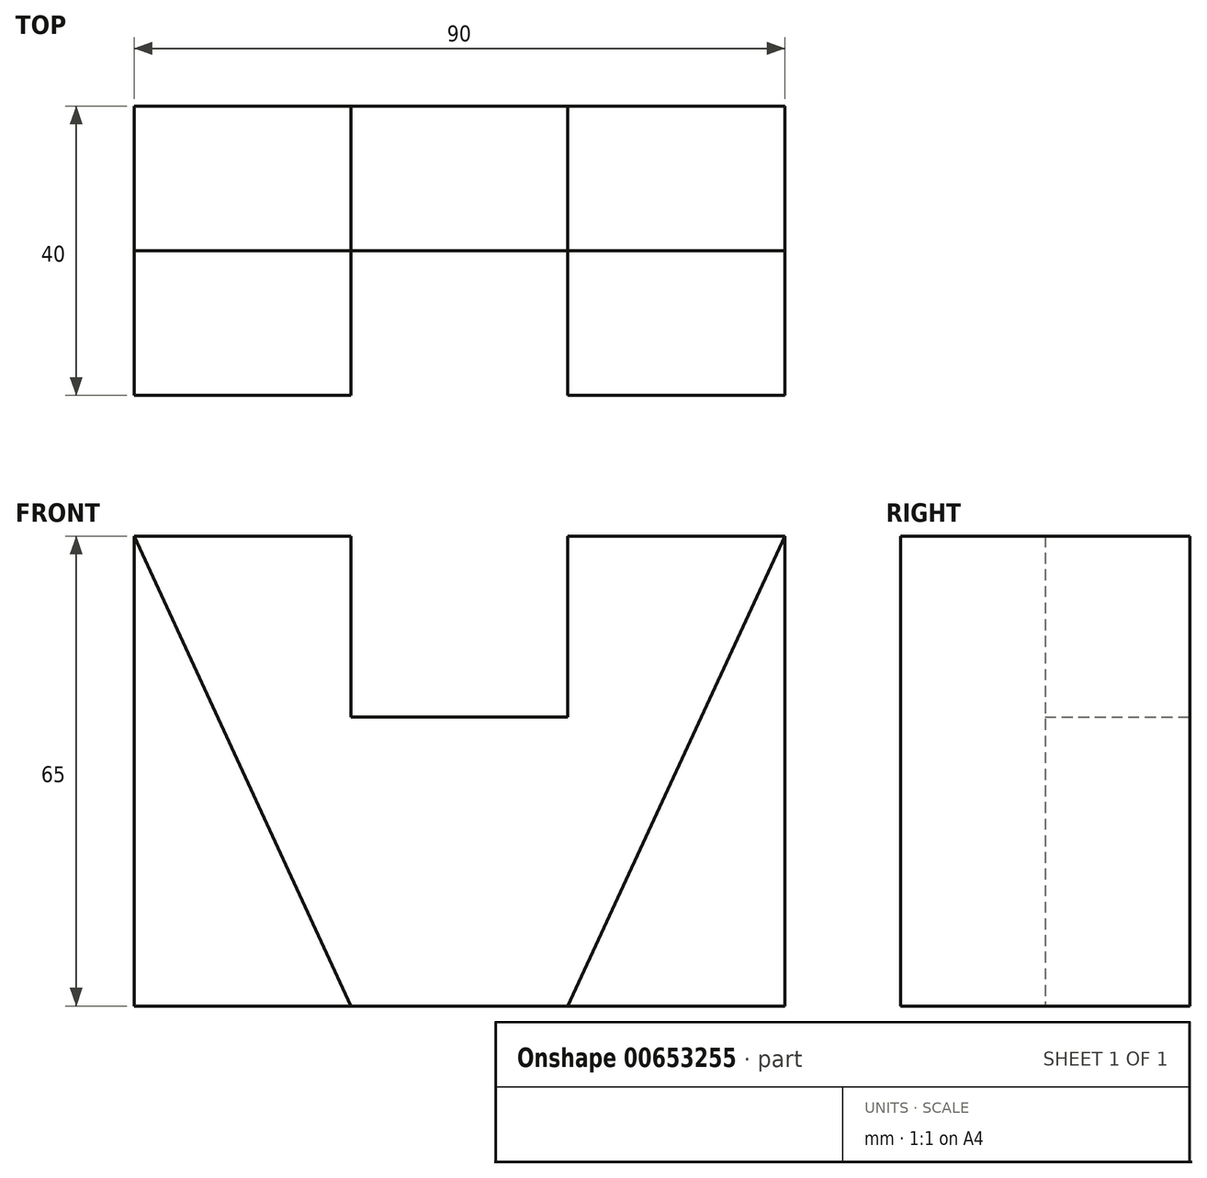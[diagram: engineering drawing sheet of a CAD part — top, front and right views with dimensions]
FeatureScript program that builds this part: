
annotation { "Feature Type Name" : "Feature", "Feature Type Description" : "" }
export const myFeature = defineFeature(function(context is Context, id is Id, definition is map)
    precondition{}
    {
        {
            var Q0;
            Q0=qCreatedBy(makeId("Front.planeOp"),FACE);
            var sketch = newSketch(context, id + "F0", { "sketchPlane" : qUnion([Q0])});
            skLineSegment(sketch, "E0.bottom", {"start": v(-45, 32.5) * mm, "end": v(-15, 32.5) * mm});
            skLineSegment(sketch, "E0.top", {"start": v(-45, -32.5) * mm, "end": v(45, -32.5) * mm});
            skLineSegment(sketch, "E0.left", {"start": v(-45, 32.5) * mm, "end": v(-45, -32.5) * mm});
            skLineSegment(sketch, "E0.right", {"start": v(45, 32.5) * mm, "end": v(45, -32.5) * mm});
            skPoint(sketch, "E0.middle", {"position": v(0, 0) * mm});
            skLineSegment(sketch, "E1.top", {"start": v(-15, 7.5) * mm, "end": v(15, 7.5) * mm});
            skLineSegment(sketch, "E1.left", {"start": v(-15, 32.5) * mm, "end": v(-15, 7.5) * mm});
            skLineSegment(sketch, "E1.right", {"start": v(15, 32.5) * mm, "end": v(15, 7.5) * mm});
            skPoint(sketch, "E1.middle", {"position": v(0, 20) * mm});
            skLineSegment(sketch, "E2.trimOffspring", {"start": v(15, 32.5) * mm, "end": v(45, 32.5) * mm});
            skSolve(sketch);
        }
        {
            var Q0;
            Q0=makeQuery(id+"F0.imprint","IMPRINT",FACE,{"disambiguationData":[TD([[makeQuery(id+"F0.imprint","IMPRINT",EDGE,{"derivedFrom":sQuery(id+"F0.wireOp",EDGE,"E0.bottom")}),-1.0]])]});
            extrude(context, id + "F1", {"entities" : qUnion([Q0]), "depth" : 20 * mm, "offsetDistance" : 25 * mm});
        }
        {
            var Q0;
            Q0=makeQuery(id+"F1.opExtrude","CAP_FACE",FACE,{"disambiguationData":[OSD([sQuery(id+"F0.wireOp",EDGE,"E0.bottom"),sQuery(id+"F0.wireOp",EDGE,"E0.top"),sQuery(id+"F0.wireOp",EDGE,"E0.left"),sQuery(id+"F0.wireOp",EDGE,"E0.right"),sQuery(id+"F0.wireOp",EDGE,"E1.top"),sQuery(id+"F0.wireOp",EDGE,"E1.left"),sQuery(id+"F0.wireOp",EDGE,"E1.right"),sQuery(id+"F0.wireOp",EDGE,"E2.trimOffspring")])],"isStart":false});
            var sketch = newSketch(context, id + "F2", { "sketchPlane" : qUnion([Q0])});
            skLineSegment(sketch, "E3", {"start": v(-45, 32.5) * mm, "end": v(-15, -32.5) * mm});
            skLineSegment(sketch, "E4", {"start": v(45, 32.5) * mm, "end": v(15, -32.5) * mm});
            skSolve(sketch);
        }
        {
            var Q0;
            {var subQ0=sQuery(id+"F2.wireOp",EDGE,"E4");Q0=makeQuery(id+"F2.imprint","IMPRINT",FACE,{"disambiguationData":[TD([[makeQuery(id+"F2.imprint","IMPRINT",EDGE,{"derivedFrom":subQ0}),1.0]])]});}
            var Q1;
            {var subQ0=sQuery(id+"F2.wireOp",EDGE,"E3");Q1=makeQuery(id+"F2.imprint","IMPRINT",FACE,{"disambiguationData":[TD([[makeQuery(id+"F2.imprint","IMPRINT",EDGE,{"derivedFrom":subQ0}),-1.0]])]});}
            extrude(context, id + "F3", {"entities" : qUnion([Q0, Q1]), "operationType" : NewBodyOperationType.ADD, "depth" : 20 * mm, "offsetDistance" : 25 * mm});
        }
    });
